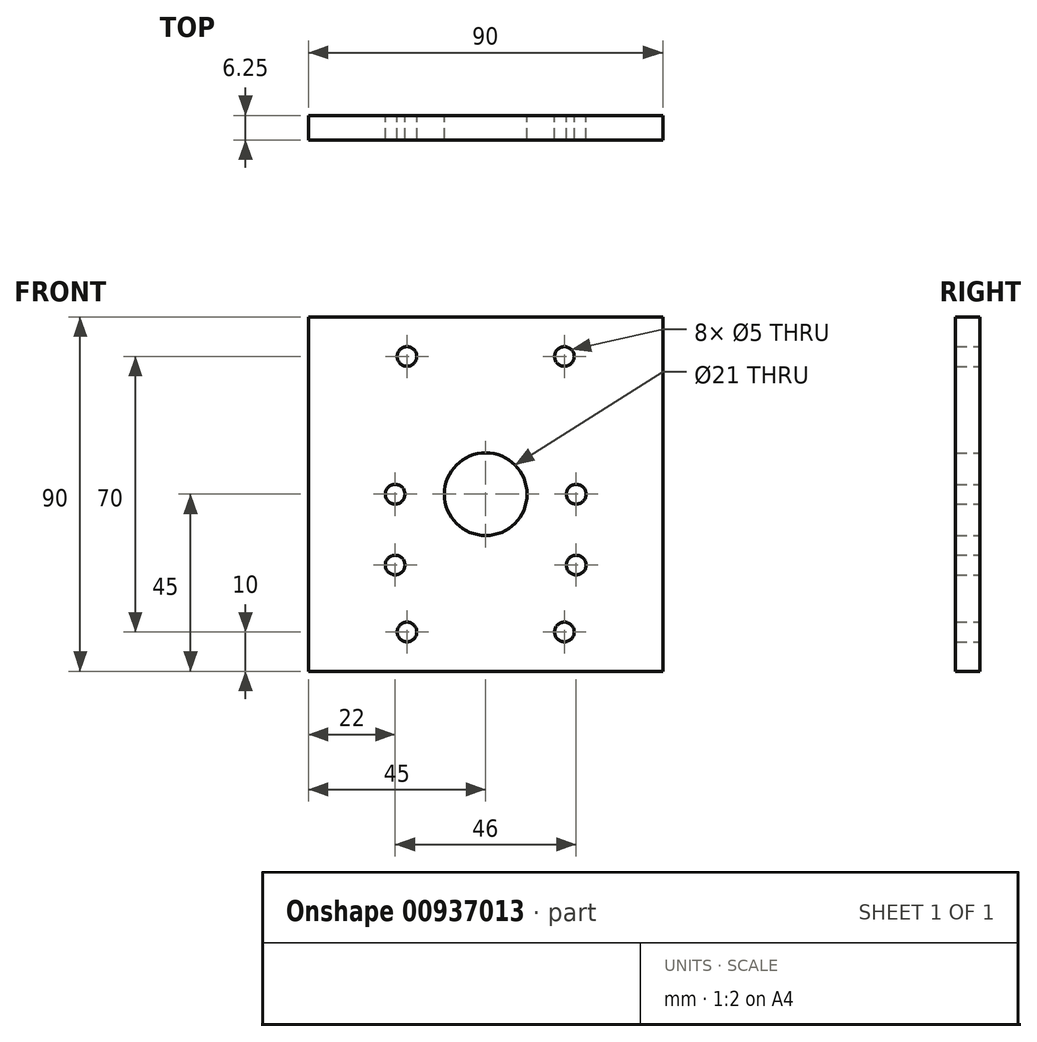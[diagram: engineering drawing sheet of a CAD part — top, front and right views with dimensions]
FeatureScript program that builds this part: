
annotation { "Feature Type Name" : "Feature", "Feature Type Description" : "" }
export const myFeature = defineFeature(function(context is Context, id is Id, definition is map)
    precondition{}
    {
        {
            var Q0;
            Q0=qCreatedBy(makeId("Front.planeOp"),FACE);
            var sketch = newSketch(context, id + "F0", { "sketchPlane" : qUnion([Q0])});
            skLineSegment(sketch, "E0.bottom", {"start": v(45, 45) * mm, "end": v(-45, 45) * mm});
            skLineSegment(sketch, "E0.top", {"start": v(45, -45) * mm, "end": v(-45, -45) * mm});
            skLineSegment(sketch, "E0.left", {"start": v(45, 45) * mm, "end": v(45, -45) * mm});
            skLineSegment(sketch, "E0.right", {"start": v(-45, 45) * mm, "end": v(-45, -45) * mm});
            skPoint(sketch, "E0.middle", {"position": v(0, 0) * mm});
            skCircle(sketch, "E1", {"center": v(0, 0) * mm, "radius": 10.5 * mm});
            skLineSegment(sketch, "E2", {"start": v(-45, 35) * mm, "end": v(45, 35) * mm, "construction": true});
            skLineSegment(sketch, "E3", {"start": v(-45, -35) * mm, "end": v(45, -35) * mm, "construction": true});
            skLineSegment(sketch, "E4", {"start": v(0, 45) * mm, "end": v(0, -45) * mm, "construction": true});
            skLineSegment(sketch, "E5", {"start": v(-20, 45) * mm, "end": v(-20, -45) * mm, "construction": true});
            skLineSegment(sketch, "E6", {"start": v(20, 45) * mm, "end": v(20, -45) * mm, "construction": true});
            skCircle(sketch, "E7", {"center": v(20, 35) * mm, "radius": 2.5 * mm});
            skCircle(sketch, "E8", {"center": v(-20, 35) * mm, "radius": 2.5 * mm});
            skCircle(sketch, "E9", {"center": v(-20, -35) * mm, "radius": 2.5 * mm});
            skCircle(sketch, "E10", {"center": v(20, -35) * mm, "radius": 2.5 * mm});
            skLineSegment(sketch, "E11.bottom", {"start": v(23, -18) * mm, "end": v(-23, -18) * mm, "construction": true});
            skLineSegment(sketch, "E11.top", {"start": v(23, 0) * mm, "end": v(-23, 0) * mm, "construction": true});
            skLineSegment(sketch, "E11.left", {"start": v(23, -18) * mm, "end": v(23, 0) * mm, "construction": true});
            skLineSegment(sketch, "E11.right", {"start": v(-23, -18) * mm, "end": v(-23, 0) * mm, "construction": true});
            skPoint(sketch, "E11.middle", {"position": v(0, -9) * mm});
            skCircle(sketch, "E12", {"center": v(-23, 0) * mm, "radius": 2.5 * mm});
            skCircle(sketch, "E13", {"center": v(23, 0) * mm, "radius": 2.5 * mm});
            skCircle(sketch, "E14", {"center": v(-23, -18) * mm, "radius": 2.5 * mm});
            skCircle(sketch, "E15", {"center": v(23, -18) * mm, "radius": 2.5 * mm});
            skSolve(sketch);
        }
        {
            var Q0;
            Q0=makeQuery(id+"F0.imprint","IMPRINT",FACE,{"disambiguationData":[TD([[makeQuery(id+"F0.imprint","IMPRINT",EDGE,{"derivedFrom":sQuery(id+"F0.wireOp",EDGE,"E0.bottom")}),1.0]])]});
            extrude(context, id + "F1", {"entities" : qUnion([Q0]), "depth" : 6.25 * mm, "offsetDistance" : 25 * mm});
        }
    });
